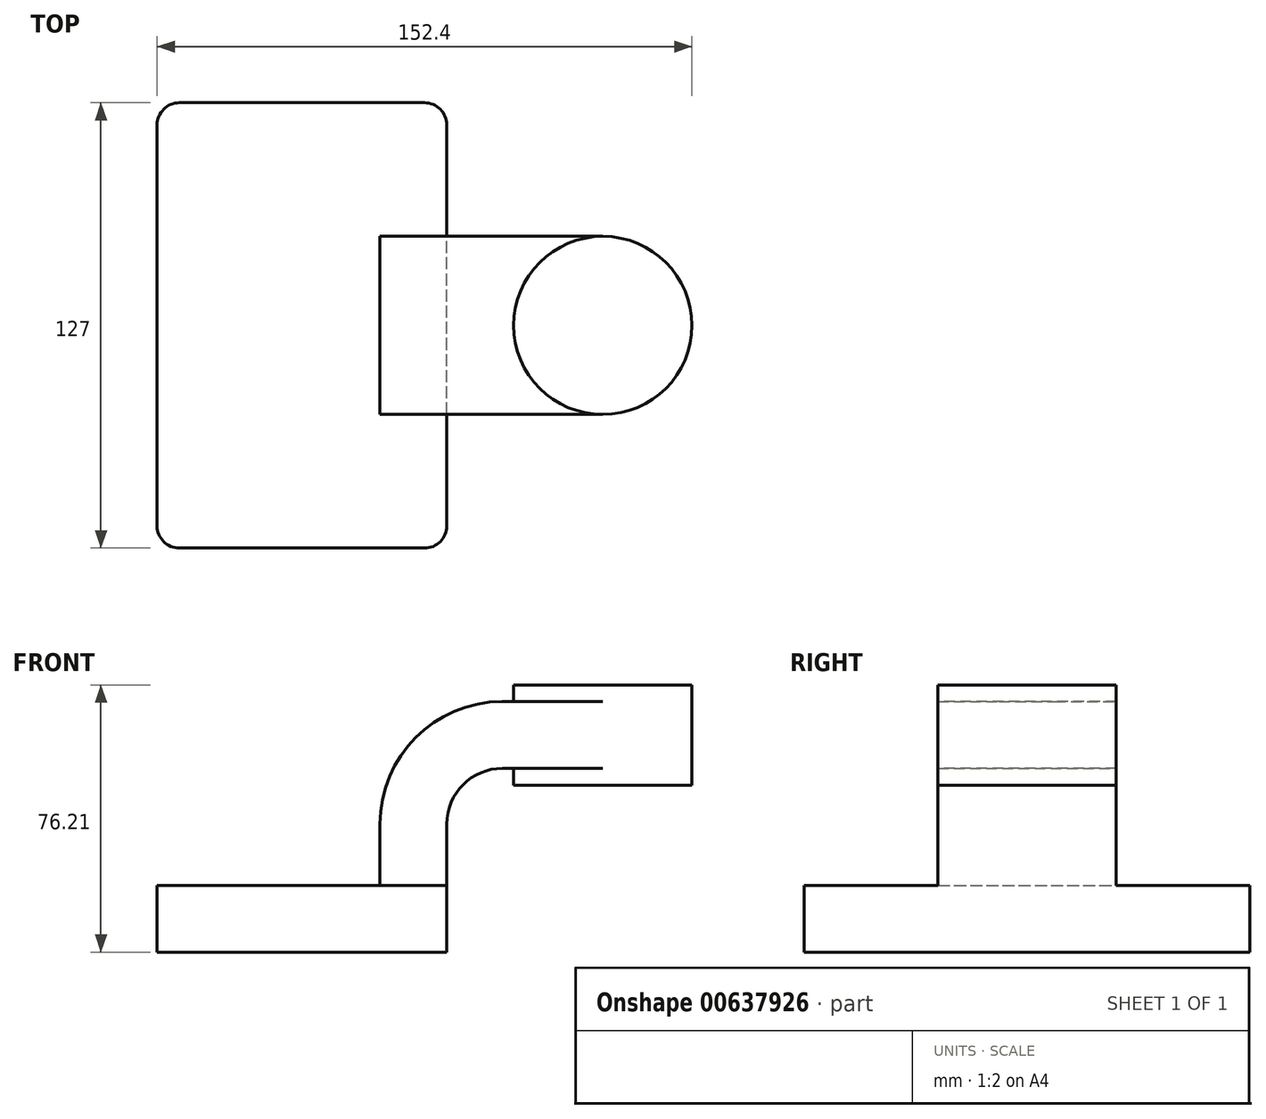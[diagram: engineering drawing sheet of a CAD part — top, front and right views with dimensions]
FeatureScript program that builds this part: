
annotation { "Feature Type Name" : "Feature", "Feature Type Description" : "" }
export const myFeature = defineFeature(function(context is Context, id is Id, definition is map)
    precondition{}
    {
        {
            var Q0;
            Q0=qCreatedBy(makeId("Front.planeOp"),FACE);
            var sketch = newSketch(context, id + "F0", { "sketchPlane" : qUnion([Q0])});
            skLineSegment(sketch, "E0.bottom", {"start": v(41.27, 9.53) * mm, "end": v(-41.28, 9.53) * mm});
            skLineSegment(sketch, "E0.top", {"start": v(41.28, -9.52) * mm, "end": v(-41.27, -9.52) * mm});
            skLineSegment(sketch, "E0.left", {"start": v(41.28, 9.53) * mm, "end": v(41.28, -9.52) * mm});
            skLineSegment(sketch, "E0.right", {"start": v(-41.28, 9.53) * mm, "end": v(-41.27, -9.52) * mm});
            skPoint(sketch, "E0.middle", {"position": v(0, 0) * mm});
            skLineSegment(sketch, "E1.bottom", {"start": v(60.33, 38.1) * mm, "end": v(111.13, 38.1) * mm});
            skLineSegment(sketch, "E1.top", {"start": v(60.33, 66.68) * mm, "end": v(111.13, 66.68) * mm});
            skLineSegment(sketch, "E1.left", {"start": v(60.33, 38.1) * mm, "end": v(60.33, 66.67) * mm});
            skLineSegment(sketch, "E1.right", {"start": v(111.13, 38.1) * mm, "end": v(111.13, 66.67) * mm});
            skPoint(sketch, "E1.middle", {"position": v(85.73, 52.39) * mm});
            skLineSegment(sketch, "E2", {"start": v(41.27, 9.53) * mm, "end": v(41.27, 27) * mm});
            skArc(sketch, "E3", {"start": v(41.28, 27) * mm, "mid": v(45.92, 38.23) * mm, "end": v(57.15, 42.88) * mm});
            skLineSegment(sketch, "E4", {"start": v(57.15, 42.88) * mm, "end": v(85.73, 42.88) * mm});
            skLineSegment(sketch, "E5.0", {"start": v(57.15, 61.93) * mm, "end": v(85.73, 61.93) * mm});
            skArc(sketch, "E5.1", {"start": v(22.23, 27) * mm, "mid": v(32.45, 51.7) * mm, "end": v(57.15, 61.93) * mm});
            skLineSegment(sketch, "E5.2", {"start": v(22.23, 9.53) * mm, "end": v(22.23, 27) * mm});
            skFitSpline(sketch, "E6", {"points": [v(-41.28, 9.53) * mm, v(57.15, 61.93) * mm], "startDerivative": vector(-1.15, 100.32) * mm, "endDerivative": vector(171.45, 0.35) * mm});
            skLineSegment(sketch, "E7", {"start": v(85.73, 66.68) * mm, "end": v(85.73, 38.1) * mm});
            skSolve(sketch);
        }
        {
            var Q0;
            Q0=makeQuery(id+"F0.imprint","IMPRINT",FACE,{"disambiguationData":[TD([[makeQuery(id+"F0.imprint","IMPRINT",EDGE,{"derivedFrom":sQuery(id+"F0.wireOp",EDGE,"E0.top")}),-1.0]])]});
            extrude(context, id + "F1", {"entities" : qUnion([Q0]), "endBound" : BoundingType.SYMMETRIC, "depth" : 127 * mm, "offsetDistance" : 25.4 * mm});
        }
        {
            var Q0;
            {var subQ1=sQuery(id+"F0.wireOp",EDGE,"E2");Q0=makeQuery(id+"F0.imprint","IMPRINT",FACE,{"disambiguationData":[TD([[makeQuery(id+"F0.imprint","IMPRINT",EDGE,{"derivedFrom":subQ1}),1.0]])]});}
            var Q1;
            {var subQ0=sQuery(id+"F0.wireOp",EDGE,"ttCeC85g-Ie9X-q9nb-LDQa-Nz597PCsuaAd");Q1=makeQuery(id+"F0.imprint","IMPRINT",FACE,{"disambiguationData":[TD([[makeQuery(id+"F0.imprint","IMPRINT",EDGE,{"derivedFrom":subQ0}),-1.0]])]});}
            var Q2;
            {var subQ0=sQuery(id+"F0.wireOp",EDGE,"E4");var subQ1=sQuery(id+"F0.wireOp",EDGE,"E1.left");var subQ2=makeQuery(id+"F0.imprint","INTERSECT",VERTEX,{"derivedFrom":[subQ1,subQ0]});Q2=makeQuery(id+"F0.imprint","IMPRINT",FACE,{"disambiguationData":[TD([[makeQuery(id+"F0.imprint","IMPRINT",EDGE,{"disambiguationData":[TD([[subQ2,-1.0]])],"derivedFrom":subQ1}),-1.0]])]});}
            extrude(context, id + "F2", {"entities" : qUnion([Q0, Q1, Q2]), "operationType" : NewBodyOperationType.ADD, "endBound" : BoundingType.SYMMETRIC, "depth" : 50.8 * mm, "offsetDistance" : 25.4 * mm});
        }
        {
            var Q0;
            {var subQ4=sQuery(id+"F0.wireOp",EDGE,"E5.1");Q0=makeQuery(id+"F0.imprint","IMPRINT",FACE,{"disambiguationData":[TD([[makeQuery(id+"F0.imprint","IMPRINT",EDGE,{"derivedFrom":subQ4}),1.0]])]});}
            extrude(context, id + "F3", {"entities" : qUnion([Q0]), "operationType" : NewBodyOperationType.ADD, "endBound" : BoundingType.SYMMETRIC, "depth" : 15.88 * mm, "offsetDistance" : 25.4 * mm});
        }
        {
            var Q0;
            {var subQ0=sQuery(id+"F0.wireOp",EDGE,"E1.right");Q0=makeQuery(id+"F0.imprint","IMPRINT",FACE,{"disambiguationData":[TD([[makeQuery(id+"F0.imprint","IMPRINT",EDGE,{"derivedFrom":subQ0}),1.0]])]});}
            var Q1;
            Q1=sQuery(id+"F0.wireOp",EDGE,"E7");
            revolve(context, id + "F4", {"operationType" : NewBodyOperationType.ADD, "entities" : qUnion([Q0]), "axis" : qUnion([Q1]), "revolveType" : RevolveType.FULL});
        }
        {
            var Q0;
            Q0=makeQuery(id+"F1.opExtrude","CAP_EDGE",EDGE,{"disambiguationData":[OSD([sQuery(id+"F0.wireOp",EDGE,"E0.left")])],"isStart":false});
            var Q1;
            Q1=makeQuery(id+"F1.opExtrude","CAP_EDGE",EDGE,{"disambiguationData":[OSD([sQuery(id+"F0.wireOp",EDGE,"E0.right")])],"isStart":false});
            var Q2;
            Q2=makeQuery(id+"F1.opExtrude","CAP_EDGE",EDGE,{"disambiguationData":[OSD([sQuery(id+"F0.wireOp",EDGE,"E0.left")])],"isStart":true});
            var Q3;
            Q3=makeQuery(id+"F1.opExtrude","CAP_EDGE",EDGE,{"disambiguationData":[OSD([sQuery(id+"F0.wireOp",EDGE,"E0.right")])],"isStart":true});
            fillet(context, id + "F5", {"entities" : qUnion([Q0, Q1, Q2, Q3]), "radius" : 6.35 * mm, "tangentPropagation" : true, "allowEdgeOverflow" : false});
        }
    });
